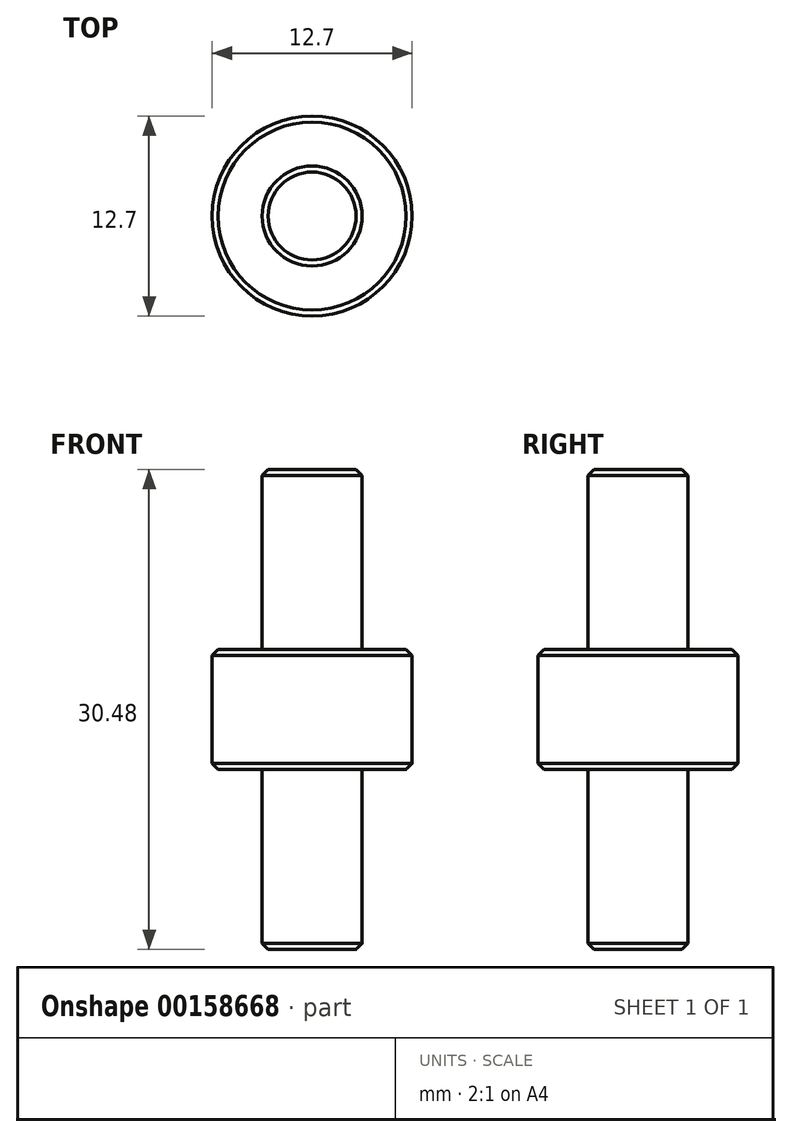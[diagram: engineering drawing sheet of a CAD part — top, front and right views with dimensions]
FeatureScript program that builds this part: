
annotation { "Feature Type Name" : "Feature", "Feature Type Description" : "" }
export const myFeature = defineFeature(function(context is Context, id is Id, definition is map)
    precondition{}
    {
        {
            var Q0;
            Q0=qCreatedBy(makeId("Top.planeOp"),FACE);
            var sketch = newSketch(context, id + "F0", { "sketchPlane" : qUnion([Q0])});
            skCircle(sketch, "E0", {"center": v(0, 0) * mm, "radius": 3.17 * mm});
            skCircle(sketch, "E1", {"center": v(0, 0) * mm, "radius": 6.35 * mm});
            skSolve(sketch);
        }
        {
            var Q0;
            Q0=makeQuery(id+"F0.imprint","IMPRINT",FACE,{"disambiguationData":[TD([[makeQuery(id+"F0.imprint","IMPRINT",EDGE,{"derivedFrom":sQuery(id+"F0.wireOp",EDGE,"E0")}),1.0]])]});
            extrude(context, id + "F1", {"entities" : qUnion([Q0]), "endBound" : BoundingType.SYMMETRIC, "depth" : 30.48 * mm});
        }
        {
            var Q0;
            Q0 = qSketchRegion(id + "F0", true);
            extrude(context, id + "F2", {"entities" : qUnion([Q0]), "operationType" : NewBodyOperationType.ADD, "endBound" : BoundingType.SYMMETRIC, "depth" : 7.62 * mm});
        }
        {
            var Q0;
            Q0=makeQuery(id+"F2.opExtrude","CAP_EDGE",EDGE,{"disambiguationData":[OSD([sQuery(id+"F0.wireOp",EDGE,"E1")])],"isStart":false});
            var Q1;
            Q1=makeQuery(id+"F2.opExtrude","CAP_EDGE",EDGE,{"disambiguationData":[OSD([sQuery(id+"F0.wireOp",EDGE,"E1")])],"isStart":true});
            var Q2;
            Q2=makeQuery(id+"F1.opExtrude","CAP_EDGE",EDGE,{"disambiguationData":[OSD([sQuery(id+"F0.wireOp",EDGE,"E0")])],"isStart":false});
            var Q3;
            Q3=makeQuery(id+"F1.opExtrude","CAP_EDGE",EDGE,{"disambiguationData":[OSD([sQuery(id+"F0.wireOp",EDGE,"E0")])],"isStart":true});
            chamfer(context, id + "F3", {"entities" : qUnion([Q0, Q1, Q2, Q3]), "width" : 0.38 * mm, "tangentPropagation" : true});
        }
    });
